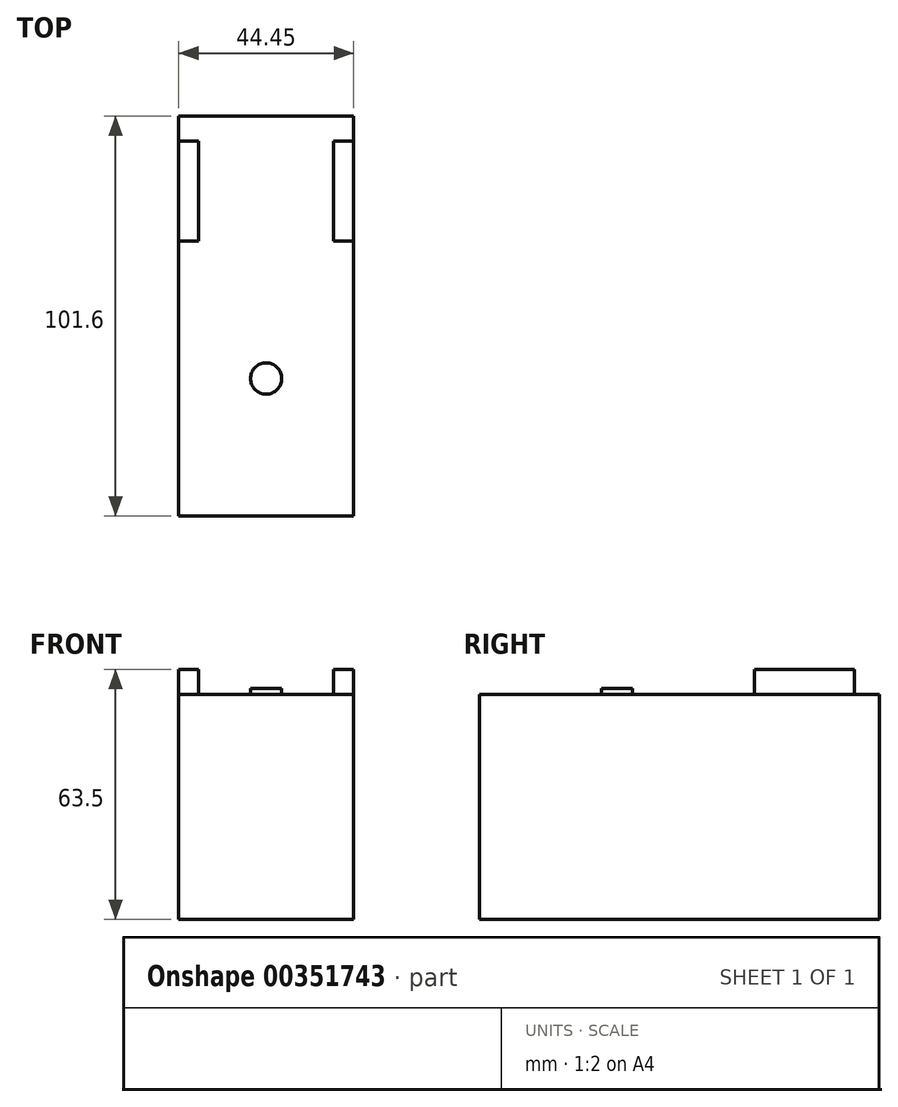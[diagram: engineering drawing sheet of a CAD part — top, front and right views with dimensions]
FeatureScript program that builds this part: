
annotation { "Feature Type Name" : "Feature", "Feature Type Description" : "" }
export const myFeature = defineFeature(function(context is Context, id is Id, definition is map)
    precondition{}
    {
        {
            var Q0;
            Q0=qCreatedBy(makeId("Front.planeOp"),FACE);
            var sketch = newSketch(context, id + "F0", { "sketchPlane" : qUnion([Q0])});
            skLineSegment(sketch, "E0", {"start": v(0, 0) * mm, "end": v(0, 57.15) * mm});
            skLineSegment(sketch, "E1", {"start": v(0, 57.15) * mm, "end": v(44.45, 57.15) * mm});
            skLineSegment(sketch, "E2", {"start": v(44.45, 57.15) * mm, "end": v(44.45, 0) * mm});
            skLineSegment(sketch, "E3", {"start": v(44.45, 0) * mm, "end": v(0, 0) * mm});
            skSolve(sketch);
        }
        {
            var Q0;
            Q0 = qSketchRegion(id + "F0", true);
            extrude(context, id + "F1", {"entities" : qUnion([Q0]), "oppositeDirection" : true, "depth" : 101.6 * mm});
        }
        {
            var Q0;
            Q0=makeQuery(id+"F1.opExtrude","SWEPT_FACE",FACE,{"disambiguationData":[OSD([sQuery(id+"F0.wireOp",EDGE,"E0")])]});
            var sketch = newSketch(context, id + "F2", { "sketchPlane" : qUnion([Q0])});
            skPoint(sketch, "E4", {"position": v(-95.25, 57.15) * mm});
            skLineSegment(sketch, "E5", {"start": v(-95.25, 57.15) * mm, "end": v(-69.85, 57.15) * mm});
            skLineSegment(sketch, "E6", {"start": v(-69.85, 57.15) * mm, "end": v(-69.85, 63.5) * mm});
            skLineSegment(sketch, "E7", {"start": v(-69.85, 63.5) * mm, "end": v(-95.25, 63.5) * mm});
            skLineSegment(sketch, "E8", {"start": v(-95.25, 63.5) * mm, "end": v(-95.25, 57.15) * mm});
            skSolve(sketch);
        }
        {
            var Q0;
            Q0 = qSketchRegion(id + "F2", true);
            extrude(context, id + "F3", {"entities" : qUnion([Q0]), "oppositeDirection" : true, "depth" : 44.45 * mm});
        }
        {
            var Q0;
            Q0=makeQuery(id+"F3.opExtrude","SWEPT_FACE",FACE,{"disambiguationData":[OSD([sQuery(id+"F2.wireOp",EDGE,"E7")])]});
            var sketch = newSketch(context, id + "F4", { "sketchPlane" : qUnion([Q0])});
            skPoint(sketch, "E9", {"position": v(5.08, 95.25) * mm});
            skPoint(sketch, "E10", {"position": v(5.08, 69.85) * mm});
            skLineSegment(sketch, "E11", {"start": v(5.08, 95.25) * mm, "end": v(39.37, 95.25) * mm});
            skLineSegment(sketch, "E12", {"start": v(39.37, 95.25) * mm, "end": v(39.37, 69.85) * mm});
            skLineSegment(sketch, "E13", {"start": v(39.37, 69.85) * mm, "end": v(5.08, 69.85) * mm});
            skLineSegment(sketch, "E14", {"start": v(5.08, 69.85) * mm, "end": v(5.08, 95.25) * mm});
            skSolve(sketch);
        }
        {
            var Q0;
            Q0 = qSketchRegion(id + "F4", true);
            extrude(context, id + "F5", {"entities" : qUnion([Q0]), "operationType" : NewBodyOperationType.REMOVE, "oppositeDirection" : true, "depth" : 6.35 * mm});
        }
        {
            var Q0;
            Q0=makeQuery(id+"F1.opExtrude","SWEPT_FACE",FACE,{"disambiguationData":[OSD([sQuery(id+"F0.wireOp",EDGE,"E1")])]});
            var sketch = newSketch(context, id + "F6", { "sketchPlane" : qUnion([Q0])});
            skPoint(sketch, "E15", {"position": v(12.04, 0) * mm});
            skPoint(sketch, "E16", {"position": v(50.33, 0) * mm});
            skPoint(sketch, "E17", {"position": v(22.22, 34.92) * mm});
            skCircle(sketch, "E18", {"center": v(22.22, 34.92) * mm, "radius": 3.97 * mm});
            skSolve(sketch);
        }
        {
            var Q0;
            Q0 = qSketchRegion(id + "F6", true);
            extrude(context, id + "F7", {"entities" : qUnion([Q0]), "operationType" : NewBodyOperationType.ADD, "depth" : 1.59 * mm});
        }
        {
            var Q0;
            Q0 = qSketchRegion(id + "F4", true);
            extrude(context, id + "F8", {"entities" : qUnion([Q0]), "operationType" : NewBodyOperationType.REMOVE, "oppositeDirection" : true, "depth" : 6.35 * mm});
        }
    });
